# Revit family: KEUCO_59557011101
name_source: partatom
category: Allgemeines Modell
revit_build: Autodesk Revit 2016 (Build: 20150220_1215(x64)
units: mm (PartAtom-declared; Revit-internal decimal feet)

## family parameters
Arbeitsebenenbasiert = Ja
Beim Laden mit Abzugskörper schneiden = Nein
Bemaßung runder Anschluss = Durchmesser verwenden
Gemeinsam genutzt = Nein
Immer vertikal = Nein
Kann Basisbauteil für Bewehrung sein = Nein
Raumberechnungspunkt = Nein
Teiletyp = Normal

## types (1)
- 59557011101
    Artikelnummer = 59557011101
    Ausschreibungstext = KEUCO IXMO 2-Wege Ab- und Umstellventil 
mit Schlauchanschluss UP DN15, 59557011101
2–Wege Ab- und Umstellventil aus hochglanzverchromten Messing 
mit IXMO Griff Comfort und Schlauchanschluss, 
frei positionierbar, eigensicher gegen Rückfließen,
integrierter Einbautiefenausgleich von 80-110 mm,
mit Justier-Möglichkeit bei Feinmontage 
für Bedienteil und Rosette,
mit runder Rosette, Schlauchanschluss G 1/2 Zoll,
Rosettendurchmesser 90 mm, Stärke 10 mm,
Gesamtausladung 80 mm,
Fertigset bestehend aus: 
Griff, Gehäuse, Rosette (rund) und Ab- und Umstellventil,
passend für UP Funktionseinheit Art.–Nr. 59556000170
    Beschreibung = Fertigset bestehend aus:
Griff, Gehäuse, Rosette (rund) und Ab- und Umstellventil,
eigensicher gegen Rückfließen, nach DIN EN 1717,
passend für UP Funktionseinheit Art.-Nr. 59556 000170
    Breite = 45 mm  [stored 0.147638 ft]
    Gewicht = 0
    Hersteller = KEUCO
    Material = Stahl, verchromt
    Serie = Plan
    URL = https://www.keuco.com
    Verwendung = DU / WA
    Vorgabe-Ansicht = 1219 mm

note: [stored X ft] marks values corroborated as IEEE doubles in the binary element streams (Revit-internal decimal feet)

## geometry (parser evidence)
native form markers: Sweep x3
no freeform markers — native parametric forms only
